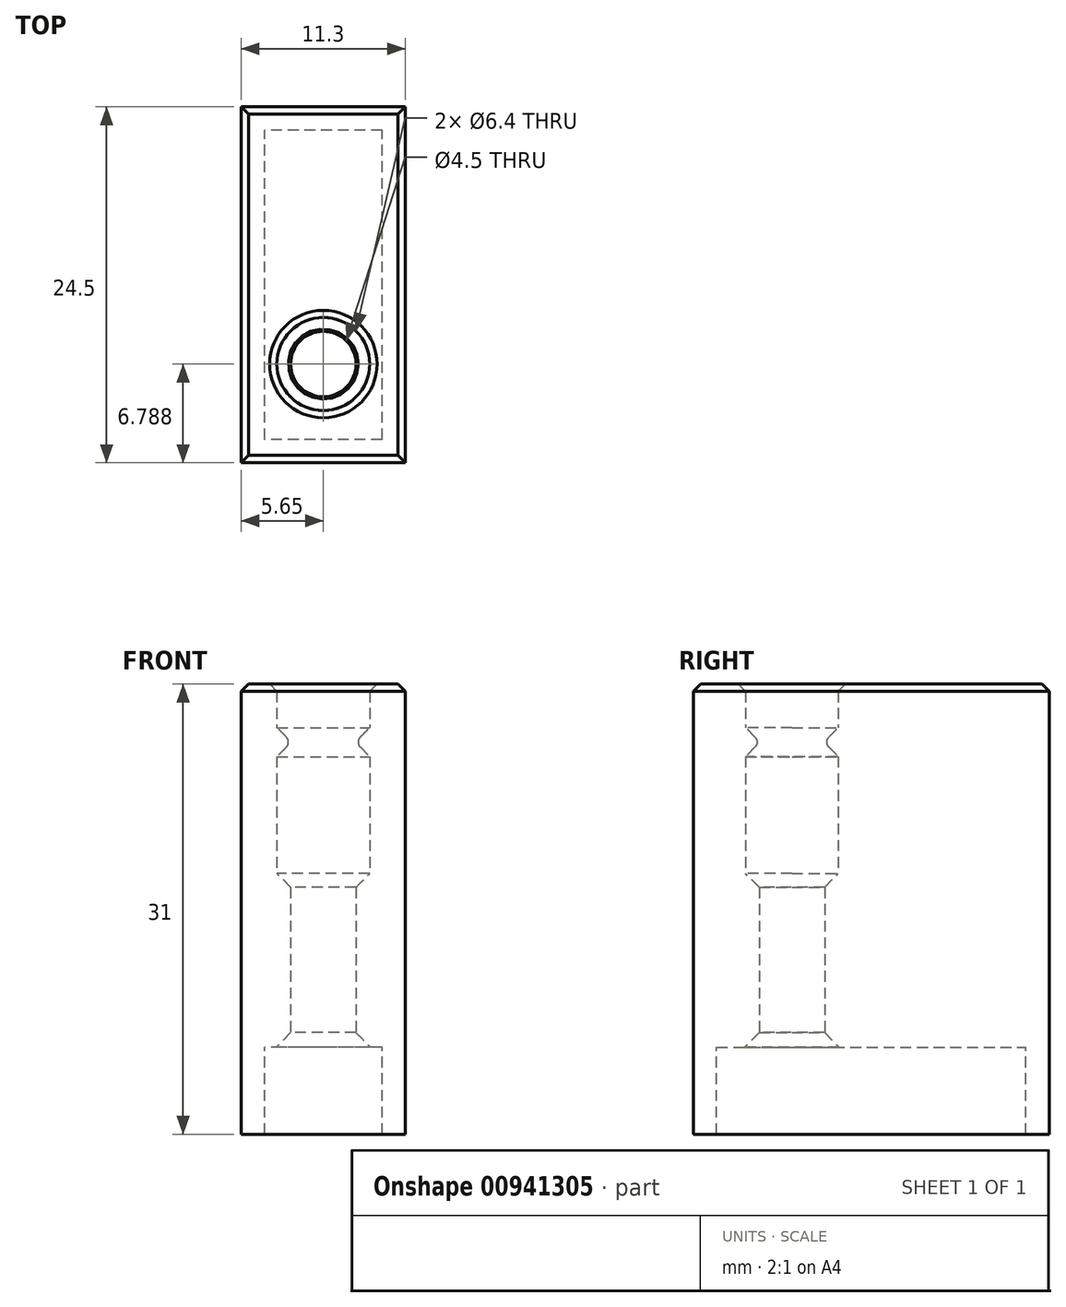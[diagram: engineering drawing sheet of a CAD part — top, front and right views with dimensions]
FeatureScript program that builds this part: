
annotation { "Feature Type Name" : "Feature", "Feature Type Description" : "" }
export const myFeature = defineFeature(function(context is Context, id is Id, definition is map)
    precondition{}
    {
        {
            var Q0;
            Q0=qCreatedBy(makeId("Top.planeOp"),FACE);
            var sketch = newSketch(context, id + "F0", { "sketchPlane" : qUnion([Q0])});
            skLineSegment(sketch, "E0.bottom", {"start": v(4.05, -10.65) * mm, "end": v(-4.05, -10.65) * mm});
            skLineSegment(sketch, "E0.top", {"start": v(4.05, 10.65) * mm, "end": v(-4.05, 10.65) * mm});
            skLineSegment(sketch, "E0.left", {"start": v(4.05, -10.65) * mm, "end": v(4.05, 10.65) * mm});
            skLineSegment(sketch, "E0.right", {"start": v(-4.05, -10.65) * mm, "end": v(-4.05, 10.65) * mm});
            skPoint(sketch, "E0.middle", {"position": v(0, 0) * mm});
            skLineSegment(sketch, "E1.0", {"start": v(-5.65, -12.25) * mm, "end": v(-5.65, 12.25) * mm});
            skLineSegment(sketch, "E1.1", {"start": v(5.65, -12.25) * mm, "end": v(-5.65, -12.25) * mm});
            skLineSegment(sketch, "E1.2", {"start": v(5.65, -12.25) * mm, "end": v(5.65, 12.25) * mm});
            skLineSegment(sketch, "E1.3", {"start": v(5.65, 12.25) * mm, "end": v(-5.65, 12.25) * mm});
            skSolve(sketch);
        }
        {
            var Q0;
            Q0=makeQuery(id+"F0.imprint","IMPRINT",FACE,{"disambiguationData":[TD([[makeQuery(id+"F0.imprint","IMPRINT",EDGE,{"derivedFrom":sQuery(id+"F0.wireOp",EDGE,"E0.bottom")}),-1.0]])]});
            var Q1;
            Q1=makeQuery(id+"F0.imprint","IMPRINT",FACE,{"disambiguationData":[TD([[makeQuery(id+"F0.imprint","IMPRINT",EDGE,{"derivedFrom":sQuery(id+"F0.wireOp",EDGE,"E0.bottom")}),1.0]])]});
            extrude(context, id + "F1", {"entities" : qUnion([Q0, Q1]), "depth" : 1 * mm, "offsetDistance" : 25 * mm});
        }
        {
            var Q0;
            Q0=makeQuery(id+"F0.imprint","IMPRINT",FACE,{"disambiguationData":[TD([[makeQuery(id+"F0.imprint","IMPRINT",EDGE,{"derivedFrom":sQuery(id+"F0.wireOp",EDGE,"E0.bottom")}),1.0]])]});
            extrude(context, id + "F2", {"entities" : qUnion([Q0]), "operationType" : NewBodyOperationType.ADD, "oppositeDirection" : true, "depth" : 6 * mm, "offsetDistance" : 25 * mm});
        }
        {
            var Q0;
            Q0=makeQuery(id+"F1.opExtrude","CAP_FACE",FACE,{"disambiguationData":[OSD([sQuery(id+"F0.wireOp",EDGE,"E1.0"),sQuery(id+"F0.wireOp",EDGE,"E1.1"),sQuery(id+"F0.wireOp",EDGE,"E1.2"),sQuery(id+"F0.wireOp",EDGE,"E1.3")])],"isStart":false});
            var sketch = newSketch(context, id + "F3", { "sketchPlane" : qUnion([Q0])});
            skCircle(sketch, "E2", {"center": v(0, -5.46) * mm, "radius": 3.2 * mm});
            skCircle(sketch, "E3", {"center": v(0, -5.46) * mm, "radius": 5.65 * mm});
            skSolve(sketch);
        }
        {
            var Q0;
            Q0=makeQuery(id+"F3.imprint","IMPRINT",FACE,{"disambiguationData":[TD([[makeQuery(id+"F3.imprint","IMPRINT",EDGE,{"derivedFrom":sQuery(id+"F3.wireOp",EDGE,"E2")}),-1.0]])]});
            var Q1;
            {var subQ5=makeQuery(id+"F1.opExtrude","CAP_EDGE",EDGE,{"disambiguationData":[OSD([sQuery(id+"F0.wireOp",EDGE,"E1.1")])],"isStart":false});Q1=makeQuery(id+"F3.imprint","IMPRINT",FACE,{"disambiguationData":[TD([[makeQuery(id+"F3.imprint","IMPRINT",EDGE,{"derivedFrom":subQ5}),-1.0]])]});}
            var Q2;
            {var subQ5=makeQuery(id+"F1.opExtrude","CAP_EDGE",EDGE,{"disambiguationData":[OSD([sQuery(id+"F0.wireOp",EDGE,"E1.3")])],"isStart":false});Q2=makeQuery(id+"F3.imprint","IMPRINT",FACE,{"disambiguationData":[TD([[makeQuery(id+"F3.imprint","IMPRINT",EDGE,{"derivedFrom":subQ5}),1.0]])]});}
            extrude(context, id + "F4", {"entities" : qUnion([Q0, Q1, Q2]), "operationType" : NewBodyOperationType.ADD, "depth" : 24 * mm, "offsetDistance" : 25 * mm});
        }
        {
            var Q0;
            Q0=makeQuery(id+"F4.boolean.opBoolean","SPLIT",FACE,{"disambiguationData":[TD([makeQuery(id+"F4.opExtrude","SWEPT_FACE",FACE,{"disambiguationData":[OSD([sQuery(id+"F3.wireOp",EDGE,"E2")])]})])],"derivedFrom":makeQuery(id+"F1.opExtrude","CAP_FACE",FACE,{"disambiguationData":[OSD([sQuery(id+"F0.wireOp",EDGE,"E1.0"),sQuery(id+"F0.wireOp",EDGE,"E1.1"),sQuery(id+"F0.wireOp",EDGE,"E1.2"),sQuery(id+"F0.wireOp",EDGE,"E1.3")])],"isStart":false})});
            extrude(context, id + "F5", {"entities" : qUnion([Q0]), "operationType" : NewBodyOperationType.REMOVE, "oppositeDirection" : true, "depth" : 28.9 * mm, "offsetDistance" : 25 * mm});
        }
        {
            var Q0;
            Q0=qCreatedBy(makeId("Right.planeOp"),FACE);
            var sketch = newSketch(context, id + "F6", { "sketchPlane" : qUnion([Q0])});
            skLineSegment(sketch, "E4", {"start": v(-10.71, 1) * mm, "end": v(-10.71, 11) * mm});
            skLineSegment(sketch, "E5", {"start": v(-0.21, 11) * mm, "end": v(-0.21, 1) * mm});
            skLineSegment(sketch, "E6", {"start": v(-8.66, 1) * mm, "end": v(-8.66, 25) * mm});
            skLineSegment(sketch, "E7", {"start": v(-2.26, 11) * mm, "end": v(-2.26, 1) * mm});
            skLineSegment(sketch, "E8.0.0", {"start": v(-10.71, 25) * mm, "end": v(-0.21, 25) * mm});
            skLineSegment(sketch, "E9", {"start": v(-5.46, 25) * mm, "end": v(-5.46, 21) * mm});
            skLineSegment(sketch, "E10", {"start": v(-5.46, 21) * mm, "end": v(-8.66, 21) * mm, "construction": true});
            skLineSegment(sketch, "E11", {"start": v(-7.66, 21) * mm, "end": v(-8.66, 22) * mm});
            skLineSegment(sketch, "E12.0.0", {"start": v(-10.65, 0) * mm, "end": v(10.65, 0) * mm});
            skLineSegment(sketch, "E12.0.2", {"start": v(10.65, 0) * mm, "end": v(-10.65, 0) * mm});
            skLineSegment(sketch, "E13", {"start": v(-7.66, 21) * mm, "end": v(-8.66, 20) * mm});
            skLineSegment(sketch, "E14.0", {"start": v(-8.66, 25) * mm, "end": v(-2.26, 25) * mm});
            skSolve(sketch);
        }
        {
            var Q0;
            {var subQ0=sQuery(id+"F6.wireOp",EDGE,"E11");Q0=makeQuery(id+"F6.imprint","IMPRINT",FACE,{"disambiguationData":[TD([[makeQuery(id+"F6.imprint","IMPRINT",EDGE,{"derivedFrom":subQ0}),1.0]])]});}
            var Q1;
            Q1=makeQuery(id+"F4.opExtrude","SWEPT_FACE",FACE,{"disambiguationData":[OSD([sQuery(id+"F3.wireOp",EDGE,"E2")])]});
            revolve(context, id + "F7", {"operationType" : NewBodyOperationType.ADD, "surfaceOperationType" : NewSurfaceOperationType.NEW, "entities" : qUnion([Q0]), "axis" : qUnion([Q1]), "revolveType" : RevolveType.FULL});
        }
        {
            var Q0;
            Q0=makeQuery(id+"F7.opRevolve","SWEPT_EDGE",EDGE,{"disambiguationData":[OSD([sQuery(id+"F6.wireOp",EDGE,"E11"),sQuery(id+"F6.wireOp",EDGE,"E13")])]});
            fillet(context, id + "F8", {"entities" : qUnion([Q0]), "radius" : .5 * mm, "tangentPropagation" : true, "allowEdgeOverflow" : false});
        }
        {
            var Q0;
            Q0=makeQuery(id+"F4.opExtrude","CAP_EDGE",EDGE,{"disambiguationData":[OSD([sQuery(id+"F0.wireOp",EDGE,"E1.0")])],"isStart":false});
            var Q1;
            Q1=makeQuery(id+"F4.opExtrude","CAP_EDGE",EDGE,{"disambiguationData":[OSD([sQuery(id+"F0.wireOp",EDGE,"E1.1")])],"isStart":false});
            var Q2;
            Q2=makeQuery(id+"F4.opExtrude","CAP_EDGE",EDGE,{"disambiguationData":[OSD([sQuery(id+"F0.wireOp",EDGE,"E1.2")])],"isStart":false});
            var Q3;
            Q3=makeQuery(id+"F4.opExtrude","CAP_EDGE",EDGE,{"disambiguationData":[OSD([sQuery(id+"F0.wireOp",EDGE,"E1.3")])],"isStart":false});
            var Q4;
            Q4=makeQuery(id+"F4.opExtrude","CAP_EDGE",EDGE,{"disambiguationData":[OSD([sQuery(id+"F3.wireOp",EDGE,"E2")])],"isStart":false});
            chamfer(context, id + "F9", {"entities" : qUnion([Q0, Q1, Q2, Q3, Q4]), "width" : .5 * mm, "tangentPropagation" : true});
        }
        {
            var Q0;
            Q0=makeQuery(id+"F0.imprint","IMPRINT",FACE,{"disambiguationData":[TD([[makeQuery(id+"F0.imprint","IMPRINT",EDGE,{"derivedFrom":sQuery(id+"F0.wireOp",EDGE,"E0.bottom")}),-1.0]])]});
            var sketch = newSketch(context, id + "F10", { "sketchPlane" : qUnion([Q0])});
            skCircle(sketch, "E15.0", {"center": v(0, -5.46) * mm, "radius": 3.2 * mm});
            skCircle(sketch, "E16", {"center": v(0, -5.46) * mm, "radius": 2.25 * mm});
            skSolve(sketch);
        }
        {
            var Q0;
            Q0=makeQuery(id+"F10.imprint","IMPRINT",FACE,{"disambiguationData":[TD([[makeQuery(id+"F10.imprint","IMPRINT",EDGE,{"derivedFrom":sQuery(id+"F10.wireOp",EDGE,"E15.0")}),1.0]])]});
            extrude(context, id + "F11", {"entities" : qUnion([Q0]), "operationType" : NewBodyOperationType.ADD, "depth" : 12 * mm, "offsetDistance" : 25 * mm});
        }
        {
            var Q0;
            Q0=makeQuery(id+"F11.opExtrude","CAP_EDGE",EDGE,{"disambiguationData":[OSD([sQuery(id+"F10.wireOp",EDGE,"E16")])],"isStart":false});
            chamfer(context, id + "F12", {"entities" : qUnion([Q0]), "width" : 1 * mm, "tangentPropagation" : true});
        }
        {
            var Q0;
            Q0=makeQuery(id+"F11.opExtrude","CAP_EDGE",EDGE,{"disambiguationData":[OSD([sQuery(id+"F10.wireOp",EDGE,"E16")])],"isStart":true});
            chamfer(context, id + "F13", {"entities" : qUnion([Q0]), "width" : 1 * mm, "tangentPropagation" : true});
        }
    });
